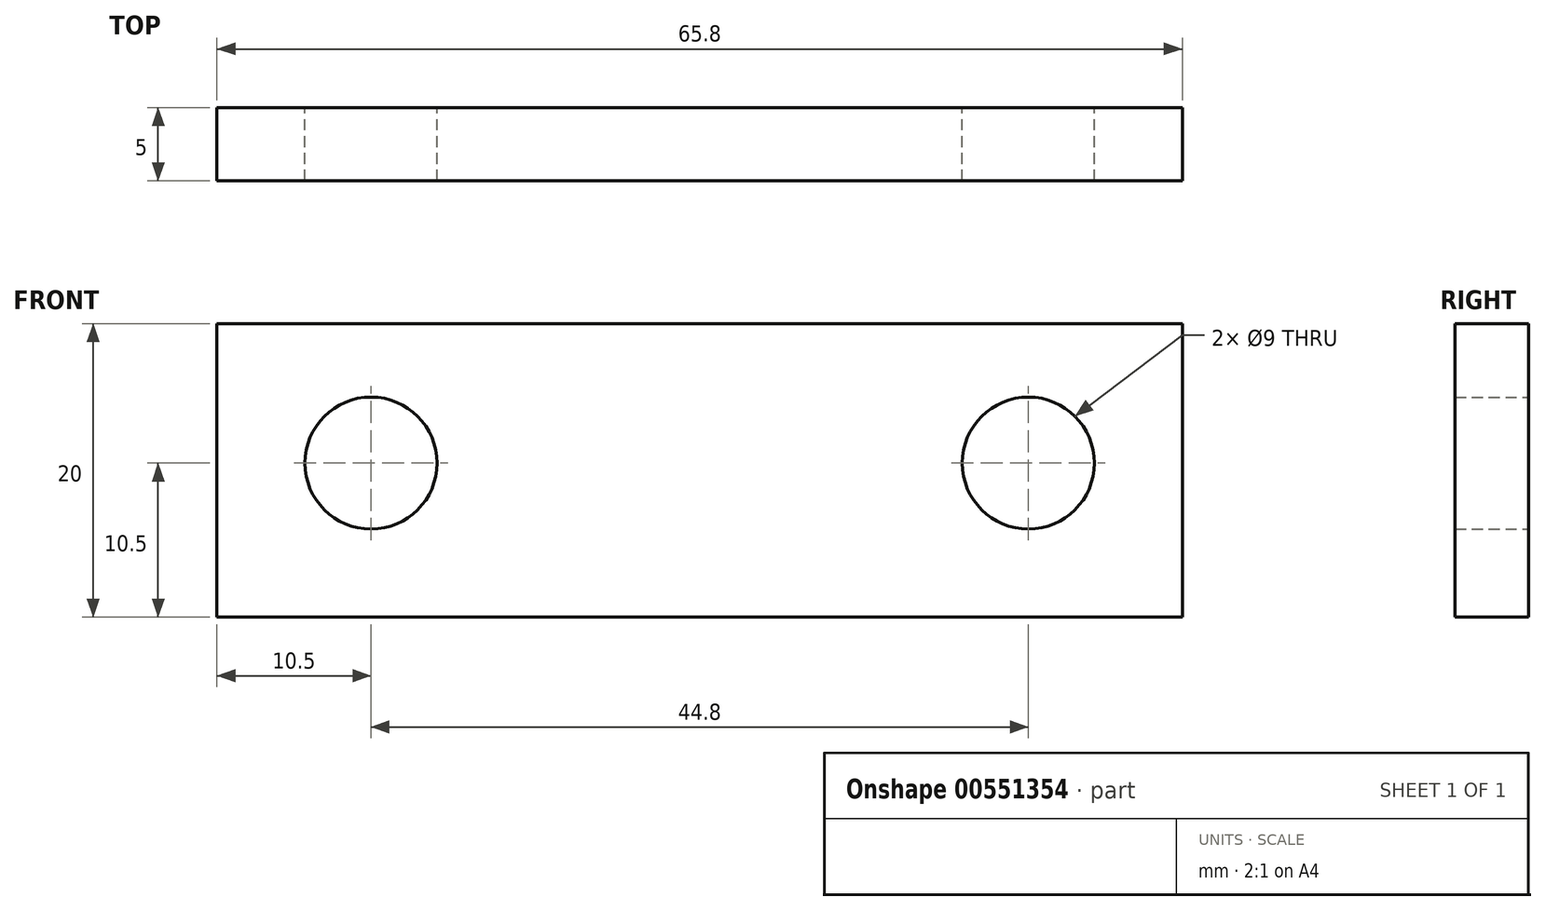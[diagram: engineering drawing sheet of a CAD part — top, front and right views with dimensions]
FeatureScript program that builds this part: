
annotation { "Feature Type Name" : "Feature", "Feature Type Description" : "" }
export const myFeature = defineFeature(function(context is Context, id is Id, definition is map)
    precondition{}
    {
        {
            var Q0;
            Q0=qCreatedBy(makeId("Front.planeOp"),FACE);
            var sketch = newSketch(context, id + "F0", { "sketchPlane" : qUnion([Q0])});
            skLineSegment(sketch, "E0.bottom", {"start": v(32.9, 10) * mm, "end": v(-32.9, 10) * mm});
            skLineSegment(sketch, "E0.top", {"start": v(32.9, -10) * mm, "end": v(-32.9, -10) * mm});
            skLineSegment(sketch, "E0.left", {"start": v(32.9, 10) * mm, "end": v(32.9, -10) * mm});
            skLineSegment(sketch, "E0.right", {"start": v(-32.9, 10) * mm, "end": v(-32.9, -10) * mm});
            skPoint(sketch, "E0.middle", {"position": v(0, 0) * mm});
            skCircle(sketch, "E1", {"center": v(-22.4, 0.5) * mm, "radius": 4.5 * mm});
            skCircle(sketch, "E2", {"center": v(22.4, 0.5) * mm, "radius": 4.5 * mm});
            skSolve(sketch);
        }
        {
            var Q0;
            Q0=makeQuery(id+"F0.imprint","IMPRINT",FACE,{"disambiguationData":[TD([[makeQuery(id+"F0.imprint","IMPRINT",EDGE,{"derivedFrom":sQuery(id+"F0.wireOp",EDGE,"E0.bottom")}),1.0]])]});
            extrude(context, id + "F1", {"entities" : qUnion([Q0]), "depth" : 5 * mm, "offsetDistance" : 25 * mm});
        }
    });
